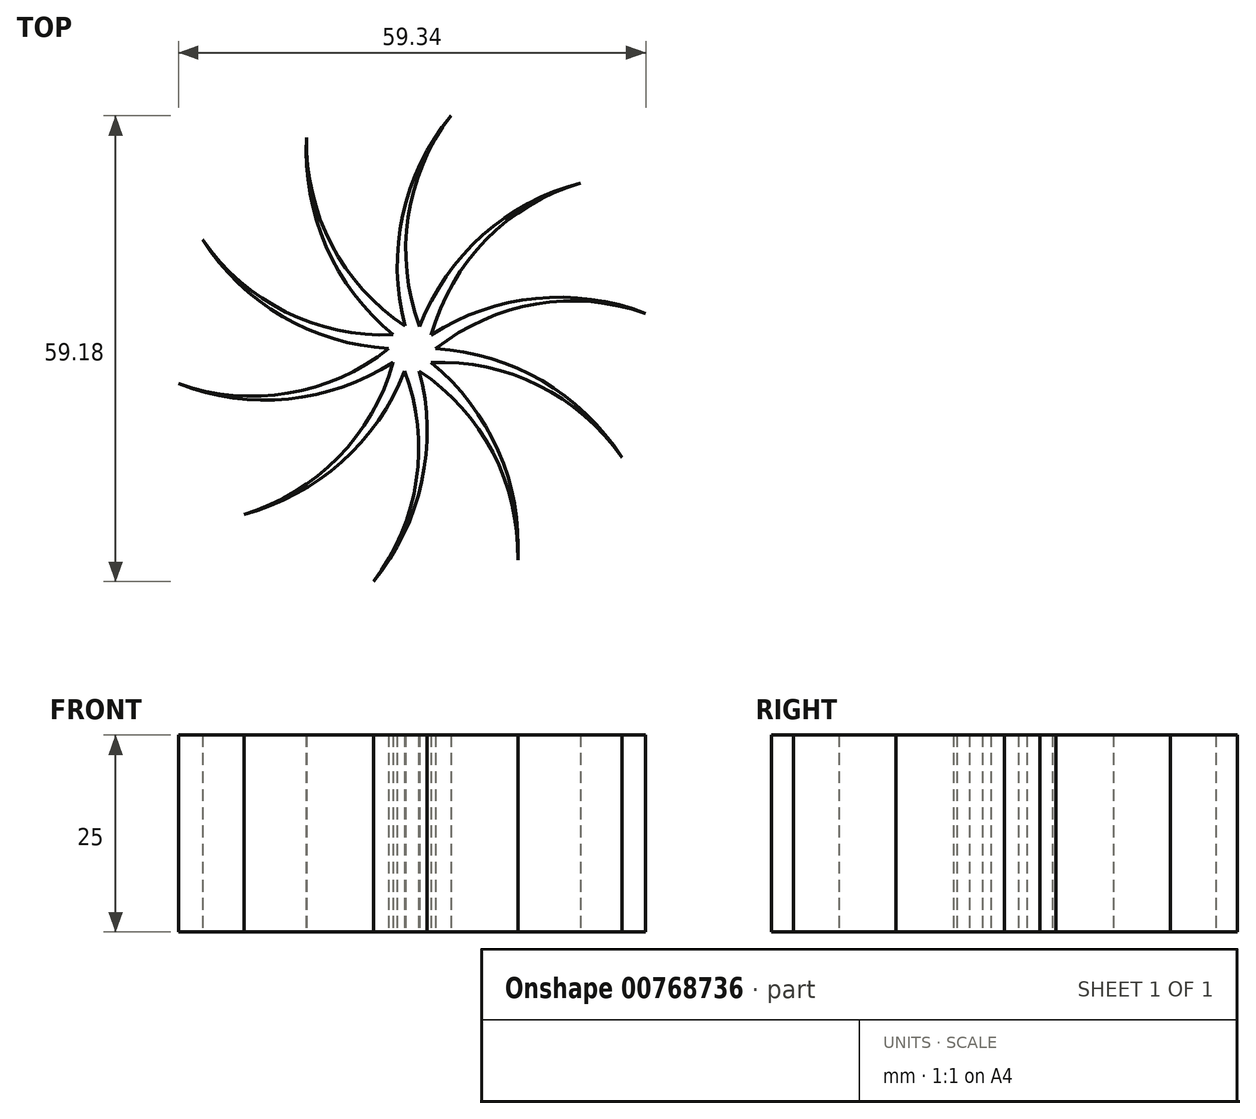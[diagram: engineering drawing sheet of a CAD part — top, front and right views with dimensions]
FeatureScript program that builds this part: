
annotation { "Feature Type Name" : "Feature", "Feature Type Description" : "" }
export const myFeature = defineFeature(function(context is Context, id is Id, definition is map)
    precondition{}
    {
        {
            var Q0;
            Q0=qCreatedBy(makeId("Top.planeOp"),FACE);
            var sketch = newSketch(context, id + "F0", { "sketchPlane" : qUnion([Q0])});
            skArc(sketch, "E0", {"start": v(21.38, 21.05) * mm, "mid": v(8.96, 14.4) * mm, "end": v(0.94, 2.83) * mm});
            skArc(sketch, "E1", {"start": v(21.38, 21.05) * mm, "mid": v(9.4, 13.84) * mm, "end": v(2.42, 1.74) * mm});
            skArc(sketch, "E2.1.0", {"start": v(4.92, 29.6) * mm, "mid": v(-1.21, 16.92) * mm, "end": v(-0.9, 2.84) * mm});
            skArc(sketch, "E2.1.1", {"start": v(4.92, 29.6) * mm, "mid": v(-0.52, 16.73) * mm, "end": v(0.94, 2.83) * mm});
            skArc(sketch, "E2.2.0", {"start": v(-13.41, 26.83) * mm, "mid": v(-10.92, 12.98) * mm, "end": v(-2.4, 1.77) * mm});
            skArc(sketch, "E2.2.1", {"start": v(-13.41, 26.83) * mm, "mid": v(-10.25, 13.23) * mm, "end": v(-0.9, 2.84) * mm});
            skArc(sketch, "E2.3.0", {"start": v(-26.62, 13.83) * mm, "mid": v(-16.47, 4.08) * mm, "end": v(-2.98, 0.02) * mm});
            skArc(sketch, "E2.3.1", {"start": v(-26.62, 13.83) * mm, "mid": v(-16.07, 4.67) * mm, "end": v(-2.4, 1.77) * mm});
            skArc(sketch, "E2.4.0", {"start": v(-29.67, -4.46) * mm, "mid": v(-15.72, -6.38) * mm, "end": v(-2.42, -1.74) * mm});
            skArc(sketch, "E2.4.1", {"start": v(-29.67, -4.46) * mm, "mid": v(-15.75, -5.66) * mm, "end": v(-2.98, 0.02) * mm});
            skArc(sketch, "E2.5.0", {"start": v(-21.38, -21.05) * mm, "mid": v(-8.96, -14.4) * mm, "end": v(-0.94, -2.83) * mm});
            skArc(sketch, "E2.5.1", {"start": v(-21.38, -21.05) * mm, "mid": v(-9.4, -13.84) * mm, "end": v(-2.42, -1.74) * mm});
            skArc(sketch, "E2.6.0", {"start": v(-4.92, -29.6) * mm, "mid": v(1.21, -16.92) * mm, "end": v(0.9, -2.84) * mm});
            skArc(sketch, "E2.6.1", {"start": v(-4.92, -29.6) * mm, "mid": v(0.52, -16.73) * mm, "end": v(-0.94, -2.83) * mm});
            skArc(sketch, "E2.7.0", {"start": v(13.41, -26.83) * mm, "mid": v(10.92, -12.98) * mm, "end": v(2.4, -1.77) * mm});
            skArc(sketch, "E2.7.1", {"start": v(13.41, -26.83) * mm, "mid": v(10.25, -13.23) * mm, "end": v(0.9, -2.84) * mm});
            skArc(sketch, "E2.8.0", {"start": v(26.62, -13.83) * mm, "mid": v(16.47, -4.08) * mm, "end": v(2.98, -0.02) * mm});
            skArc(sketch, "E2.8.1", {"start": v(26.62, -13.83) * mm, "mid": v(16.07, -4.67) * mm, "end": v(2.4, -1.77) * mm});
            skArc(sketch, "E2.9.0", {"start": v(29.67, 4.46) * mm, "mid": v(15.72, 6.38) * mm, "end": v(2.42, 1.74) * mm});
            skArc(sketch, "E2.9.1", {"start": v(29.67, 4.46) * mm, "mid": v(15.75, 5.66) * mm, "end": v(2.98, -0.02) * mm});
            skPoint(sketch, "E2.center", {"position": v(0, 0) * mm});
            skPoint(sketch, "E3.orphan", {"position": v(1.62, 1.18) * mm});
            skSolve(sketch);
        }
        {
            var Q0;
            Q0=makeQuery(id+"F0.imprint","IMPRINT",FACE,{"disambiguationData":[TD([[makeQuery(id+"F0.imprint","IMPRINT",EDGE,{"derivedFrom":sQuery(id+"F0.wireOp",EDGE,"E0")}),1.0]])]});
            extrude(context, id + "F1", {"entities" : qUnion([Q0]), "depth" : 25 * mm, "offsetDistance" : 25 * mm});
        }
    });
